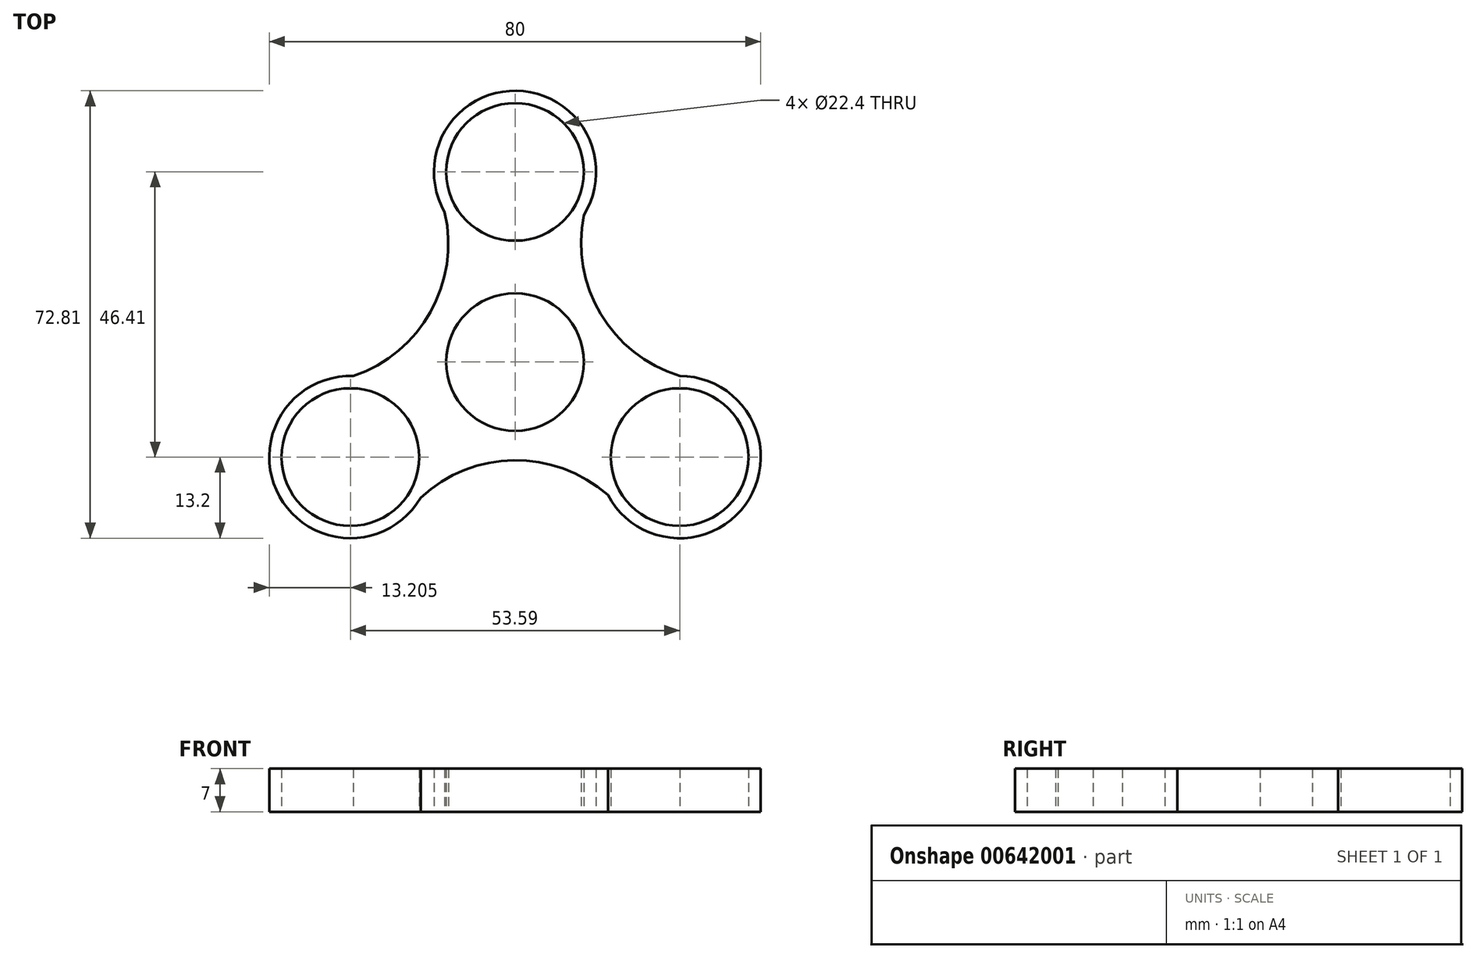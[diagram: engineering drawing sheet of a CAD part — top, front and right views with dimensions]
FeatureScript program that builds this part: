
annotation { "Feature Type Name" : "Feature", "Feature Type Description" : "" }
export const myFeature = defineFeature(function(context is Context, id is Id, definition is map)
    precondition{}
    {
        {
            var Q0;
            Q0=qCreatedBy(makeId("Top.planeOp"),FACE);
            var sketch = newSketch(context, id + "F0", { "sketchPlane" : qUnion([Q0])});
            skCircle(sketch, "E0", {"center": v(0, 0) * mm, "radius": 11.2 * mm});
            skCircle(sketch, "E1", {"center": v(0, 30.94) * mm, "radius": 11.2 * mm});
            skArc(sketch, "E2", {"start": v(11.18, 23.93) * mm, "mid": v(0.24, 44.14) * mm, "end": v(-11.43, 24.34) * mm});
            skArc(sketch, "E3.1.0", {"start": v(-26.31, -2.28) * mm, "mid": v(-38.35, -21.86) * mm, "end": v(-15.36, -22.07) * mm});
            skCircle(sketch, "E3.1.1", {"center": v(-26.8, -15.47) * mm, "radius": 11.2 * mm});
            skArc(sketch, "E3.2.0", {"start": v(15.13, -21.65) * mm, "mid": v(38.1, -22.28) * mm, "end": v(26.8, -2.27) * mm});
            skCircle(sketch, "E3.2.1", {"center": v(26.8, -15.47) * mm, "radius": 11.2 * mm});
            skArc(sketch, "E4", {"start": v(11.18, 23.93) * mm, "mid": v(13.95, 7.82) * mm, "end": v(26.8, -2.27) * mm});
            skArc(sketch, "E5.1.0", {"start": v(-26.31, -2.28) * mm, "mid": v(-13.75, 8.17) * mm, "end": v(-11.43, 24.34) * mm});
            skArc(sketch, "E5.2.0", {"start": v(15.13, -21.65) * mm, "mid": v(-0.2, -16) * mm, "end": v(-15.36, -22.07) * mm});
            skSolve(sketch);
        }
        {
            var Q0;
            Q0=makeQuery(id+"F0.imprint","IMPRINT",FACE,{"disambiguationData":[TD([[makeQuery(id+"F0.imprint","IMPRINT",EDGE,{"derivedFrom":sQuery(id+"F0.wireOp",EDGE,"E0")}),-1.0]])]});
            extrude(context, id + "F1", {"entities" : qUnion([Q0]), "depth" : 7 * mm, "offsetDistance" : 25 * mm});
        }
    });
